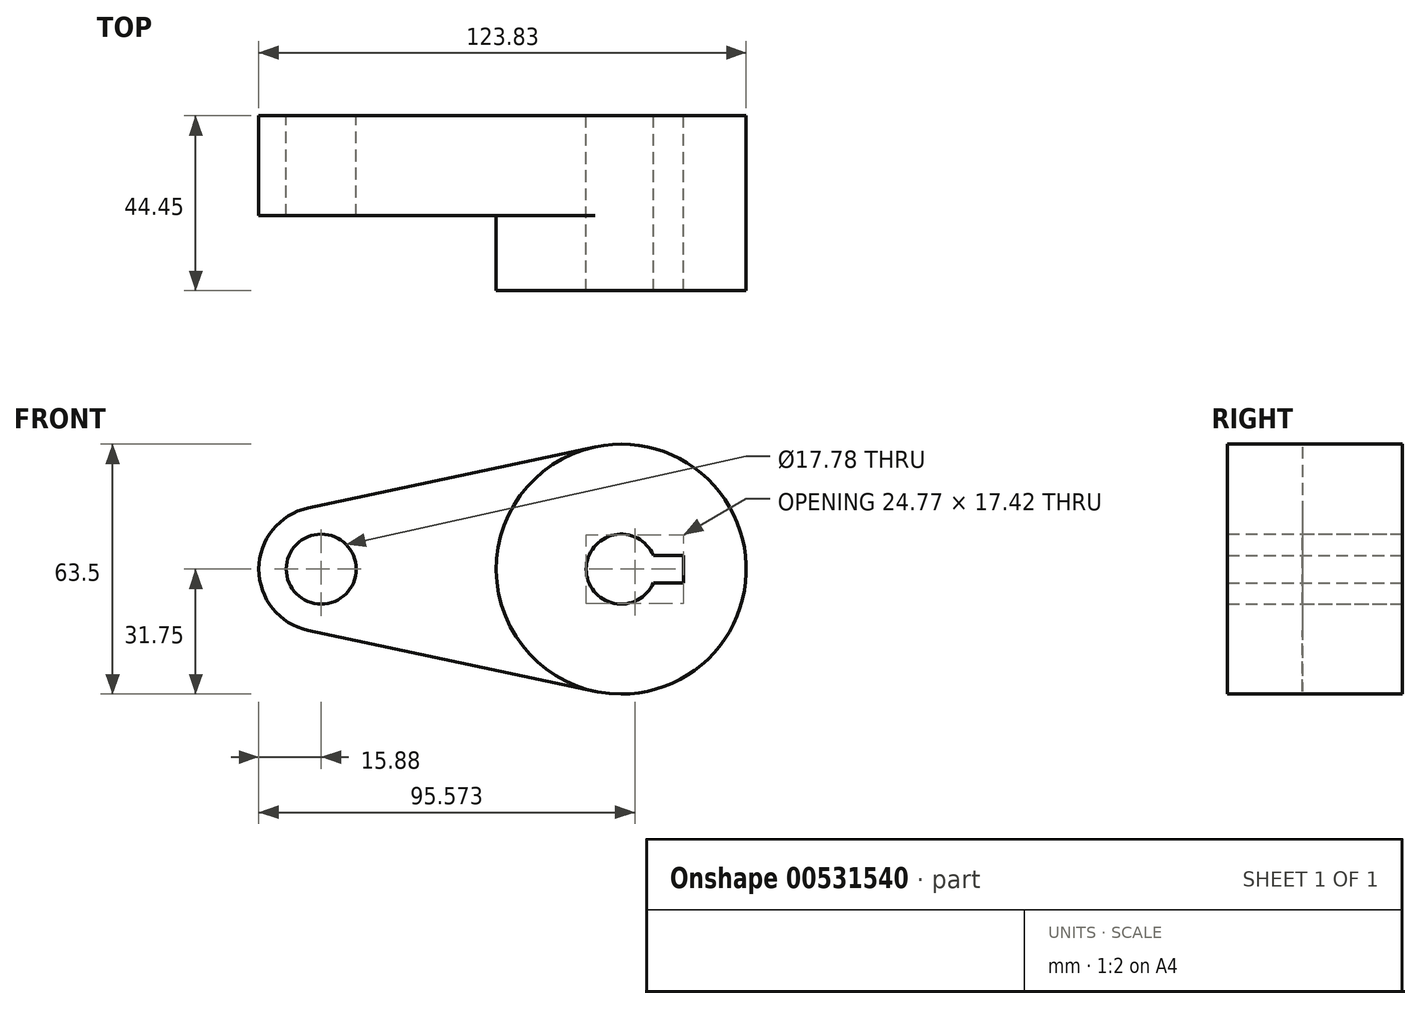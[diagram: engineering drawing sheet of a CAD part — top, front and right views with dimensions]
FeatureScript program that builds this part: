
annotation { "Feature Type Name" : "Feature", "Feature Type Description" : "" }
export const myFeature = defineFeature(function(context is Context, id is Id, definition is map)
    precondition{}
    {
        {
            var Q0;
            Q0=qCreatedBy(makeId("Front.planeOp"),FACE);
            var sketch = newSketch(context, id + "F0", { "sketchPlane" : qUnion([Q0])});
            skCircle(sketch, "E0", {"center": v(0, 0) * mm, "radius": 31.75 * mm});
            skCircle(sketch, "E1", {"center": v(-76.2, 0) * mm, "radius": 15.88 * mm});
            skLineSegment(sketch, "E2", {"start": v(-6.61, 31.05) * mm, "end": v(-79.5, 15.53) * mm});
            skLineSegment(sketch, "E3", {"start": v(-6.61, -31.05) * mm, "end": v(-79.5, -15.53) * mm});
            skCircle(sketch, "E4", {"center": v(0, 0) * mm, "radius": 8.9 * mm});
            skCircle(sketch, "E5", {"center": v(-76.2, 0) * mm, "radius": 8.9 * mm});
            skLineSegment(sketch, "E6.bottom", {"start": v(15.88, 3.5) * mm, "end": v(-15.88, 3.5) * mm});
            skLineSegment(sketch, "E6.top", {"start": v(15.88, -3.5) * mm, "end": v(-15.88, -3.5) * mm});
            skLineSegment(sketch, "E6.left", {"start": v(15.88, 3.5) * mm, "end": v(15.88, -3.5) * mm});
            skLineSegment(sketch, "E6.right", {"start": v(-15.88, 3.5) * mm, "end": v(-15.88, -3.5) * mm});
            skSolve(sketch);
        }
        {
            var Q0;
            {var subQ5=sQuery(id+"F0.wireOp",EDGE,"E6.right");Q0=makeQuery(id+"F0.imprint","IMPRINT",FACE,{"disambiguationData":[TD([[makeQuery(id+"F0.imprint","IMPRINT",EDGE,{"derivedFrom":subQ5}),1.0]])]});}
            var Q1;
            {var subQ7=sQuery(id+"F0.wireOp",EDGE,"E6.left");Q1=makeQuery(id+"F0.imprint","IMPRINT",FACE,{"disambiguationData":[TD([[makeQuery(id+"F0.imprint","IMPRINT",EDGE,{"derivedFrom":subQ7}),1.0]])]});}
            var Q2;
            {var subQ0=sQuery(id+"F0.wireOp",EDGE,"E2");Q2=makeQuery(id+"F0.imprint","IMPRINT",FACE,{"disambiguationData":[TD([[makeQuery(id+"F0.imprint","IMPRINT",EDGE,{"derivedFrom":subQ0}),1.0]])]});}
            var Q3;
            Q3=makeQuery(id+"F0.imprint","IMPRINT",FACE,{"disambiguationData":[TD([[makeQuery(id+"F0.imprint","IMPRINT",EDGE,{"derivedFrom":sQuery(id+"F0.wireOp",EDGE,"E5")}),-1.0]])]});
            extrude(context, id + "F1", {"entities" : qUnion([Q0, Q1, Q2, Q3]), "depth" : 25.4 * mm, "offsetDistance" : 25.4 * mm});
        }
        {
            var Q0;
            {var subQ5=sQuery(id+"F0.wireOp",EDGE,"E6.right");Q0=makeQuery(id+"F0.imprint","IMPRINT",FACE,{"disambiguationData":[TD([[makeQuery(id+"F0.imprint","IMPRINT",EDGE,{"derivedFrom":subQ5}),1.0]])]});}
            var Q1;
            {var subQ7=sQuery(id+"F0.wireOp",EDGE,"E6.left");Q1=makeQuery(id+"F0.imprint","IMPRINT",FACE,{"disambiguationData":[TD([[makeQuery(id+"F0.imprint","IMPRINT",EDGE,{"derivedFrom":subQ7}),1.0]])]});}
            extrude(context, id + "F2", {"entities" : qUnion([Q0, Q1]), "operationType" : NewBodyOperationType.ADD, "depth" : 44.45 * mm, "offsetDistance" : 25.4 * mm});
        }
    });
